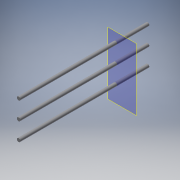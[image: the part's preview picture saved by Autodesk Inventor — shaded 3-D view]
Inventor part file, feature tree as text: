
AUTODESK INVENTOR PART (.ipt)
format: ipt  version: 2016 (Build 200138000, 138)  size: 113,152 bytes
history: native  units: in
note: dims shown in document units (in); Inventor stores cm internally (conversion verified against a paired STEP export)
features: extrude x2, sketch x2, plane x1, reference x1
ambient origin geometry x8: Origin, YZ Plane, XZ Plane, XY Plane, X Axis, Y Axis, Z Axis, Center Point
bodies: Solid1 (feature_tree)
feature tree (6):
  plane  "Work Plane1"
  extrude  "Extrusion1"  Depth=0.315in
  extrude  "Extrusion2"  Depth=2.9528in TaperAngle=0.0deg
  sketch  "Sketch1"  dims[d0=0.315in d1=0.315in]
  reference  "Reference1"
  sketch  "Sketch2"  dims[d2=0.315in d3=2.9528in d4=8.8583in d5=0.0in d6=0.0in d7=0.7874in d8=0.7874in d9=14.0in d10=0.0in]
